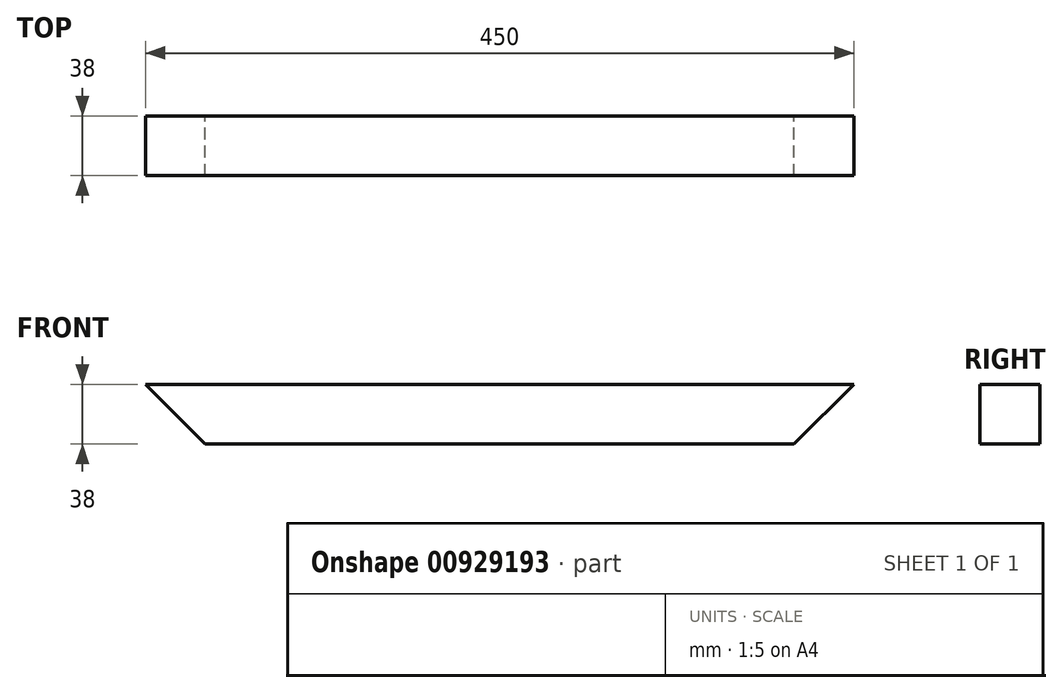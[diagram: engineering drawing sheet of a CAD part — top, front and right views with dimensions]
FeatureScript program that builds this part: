
annotation { "Feature Type Name" : "Feature", "Feature Type Description" : "" }
export const myFeature = defineFeature(function(context is Context, id is Id, definition is map)
    precondition{}
    {
        {
            var Q0;
            Q0=qCreatedBy(makeId("Front.planeOp"),FACE);
            var sketch = newSketch(context, id + "F0", { "sketchPlane" : qUnion([Q0])});
            skLineSegment(sketch, "E0", {"start": v(-169.53, 0) * mm, "end": v(280.47, 0) * mm});
            skLineSegment(sketch, "E1", {"start": v(280.47, 0) * mm, "end": v(242.47, -38) * mm});
            skLineSegment(sketch, "E2", {"start": v(242.47, -38) * mm, "end": v(-131.53, -38) * mm});
            skLineSegment(sketch, "E3", {"start": v(-131.53, -38) * mm, "end": v(-169.53, 0) * mm});
            skSolve(sketch);
        }
        {
            var Q0;
            Q0 = qSketchRegion(id + "F0", true);
            extrude(context, id + "F1", {"entities" : qUnion([Q0]), "depth" : 38 * mm, "offsetDistance" : 25 * mm});
        }
    });
